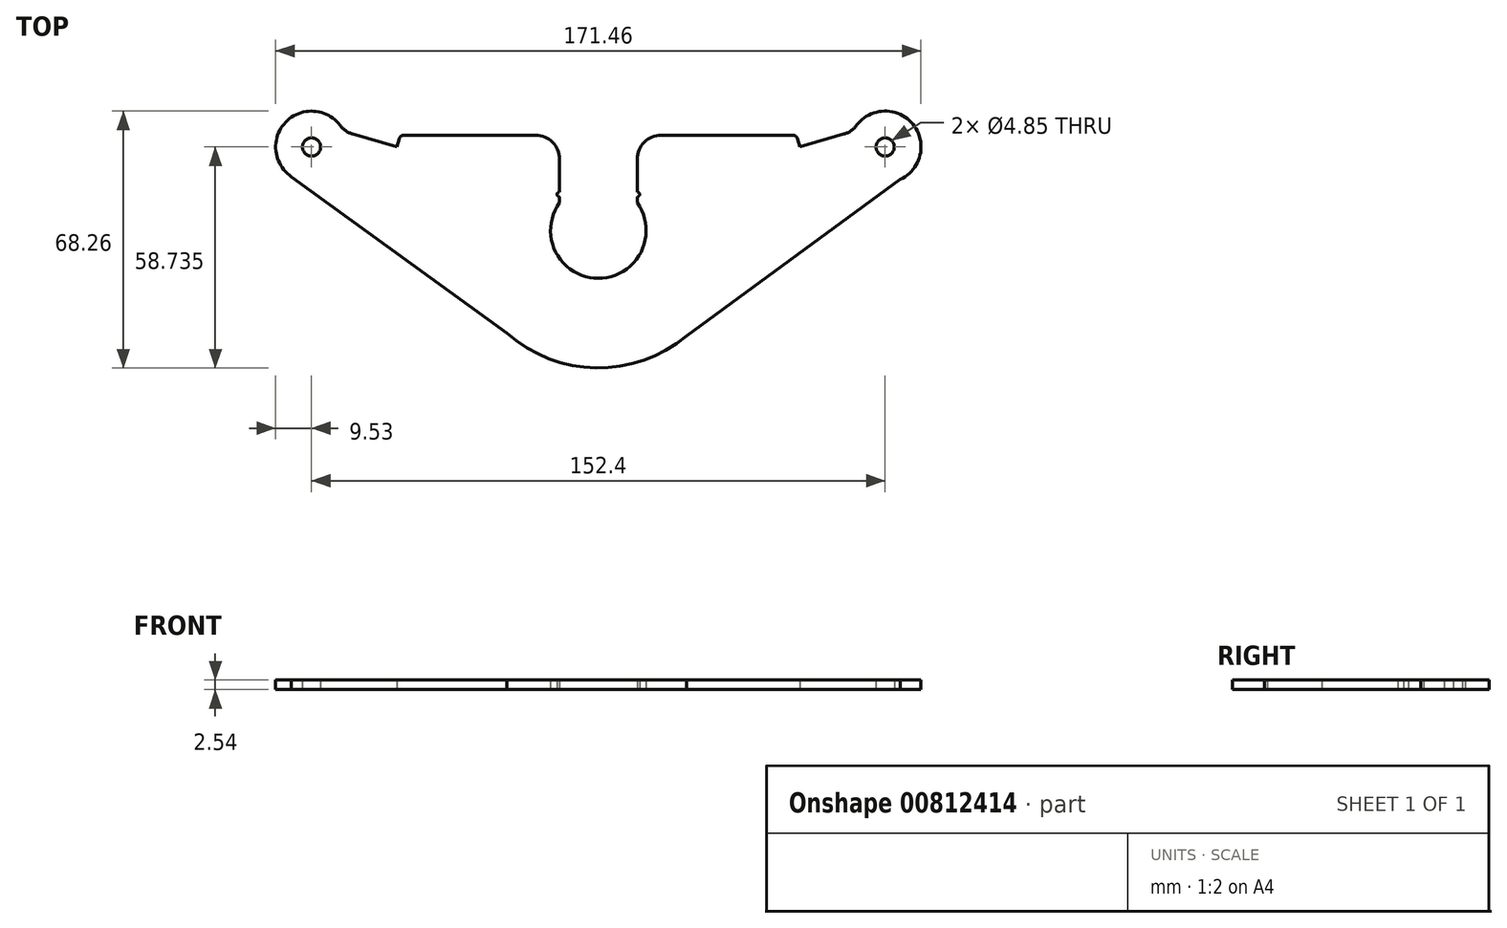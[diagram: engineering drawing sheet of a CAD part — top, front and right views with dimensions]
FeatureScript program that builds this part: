
annotation { "Feature Type Name" : "Feature", "Feature Type Description" : "" }
export const myFeature = defineFeature(function(context is Context, id is Id, definition is map)
    precondition{}
    {
        {
            var Q0;
            Q0=qCreatedBy(makeId("Top.planeOp"),FACE);
            var sketch = newSketch(context, id + "F0", { "sketchPlane" : qUnion([Q0])});
            skArc(sketch, "E0", {"start": v(-10.32, 7.4) * mm, "mid": v(0, -12.7) * mm, "end": v(10.32, 7.4) * mm});
            skCircle(sketch, "E1", {"center": v(-76.2, 22.23) * mm, "radius": 2.43 * mm});
            skCircle(sketch, "E2", {"center": v(76.2, 22.23) * mm, "radius": 2.43 * mm});
            skArc(sketch, "E3", {"start": v(-68.58, 27.94) * mm, "mid": v(-83.1, 28.8) * mm, "end": v(-81.53, 14.33) * mm});
            skArc(sketch, "E4", {"start": v(80.23, 13.6) * mm, "mid": v(83.6, 28.23) * mm, "end": v(68.58, 27.94) * mm});
            skArc(sketch, "E5", {"start": v(-24.33, -27.22) * mm, "mid": v(-0.62, -36.5) * mm, "end": v(23.39, -28.04) * mm});
            skLineSegment(sketch, "E6", {"start": v(-81.53, 14.33) * mm, "end": v(-24.33, -27.22) * mm});
            skLineSegment(sketch, "E7", {"start": v(23.39, -28.04) * mm, "end": v(83.2, 15.78) * mm});
            skLineSegment(sketch, "E8.0", {"start": v(-65.28, 25.65) * mm, "end": v(-53.54, 22.23) * mm});
            skLineSegment(sketch, "E9.0", {"start": v(53.54, 22.23) * mm, "end": v(65.28, 25.65) * mm});
            skLineSegment(sketch, "E10.left", {"start": v(10.32, 8.99) * mm, "end": v(10.32, 7.4) * mm});
            skLineSegment(sketch, "E10.right", {"start": v(-10.32, 9) * mm, "end": v(-10.32, 7.4) * mm});
            skPoint(sketch, "E10.top.end.orphan", {"position": v(-10.32, -39.66) * mm});
            skPoint(sketch, "E11.trimOffspring.end.orphan", {"position": v(10.32, -39.66) * mm});
            skPoint(sketch, "E10.bottom.end.orphan", {"position": v(-10.32, 39.66) * mm});
            skPoint(sketch, "E12.orphan", {"position": v(10.32, 39.66) * mm});
            skLineSegment(sketch, "E13", {"start": v(-10.32, 10.25) * mm, "end": v(-10.32, 18.98) * mm});
            skLineSegment(sketch, "E14", {"start": v(10.32, 10.26) * mm, "end": v(10.32, 18.98) * mm});
            skLineSegment(sketch, "E15", {"start": v(-52.9, 24.42) * mm, "end": v(-53.54, 22.23) * mm});
            skLineSegment(sketch, "E16", {"start": v(-16.67, 25.33) * mm, "end": v(-51.68, 25.33) * mm});
            skLineSegment(sketch, "E17", {"start": v(16.67, 25.33) * mm, "end": v(51.68, 25.33) * mm});
            skLineSegment(sketch, "E18", {"start": v(52.9, 24.42) * mm, "end": v(53.54, 22.23) * mm});
            skPoint(sketch, "E19.visualSharp", {"position": v(-67.6, 26.33) * mm});
            skArc(sketch, "E19.filletArc", {"start": v(-68.58, 27.94) * mm, "mid": v(-67.11, 26.53) * mm, "end": v(-65.28, 25.65) * mm});
            skPoint(sketch, "E20.visualSharp", {"position": v(67.6, 26.33) * mm});
            skArc(sketch, "E20.filletArc", {"start": v(65.28, 25.65) * mm, "mid": v(67.11, 26.53) * mm, "end": v(68.58, 27.94) * mm});
            skPoint(sketch, "E21.visualSharp", {"position": v(10.32, 25.33) * mm});
            skArc(sketch, "E21.filletArc", {"start": v(16.67, 25.33) * mm, "mid": v(12.18, 23.47) * mm, "end": v(10.32, 18.98) * mm});
            skPoint(sketch, "E22.visualSharp", {"position": v(-10.32, 25.33) * mm});
            skArc(sketch, "E22.filletArc", {"start": v(-10.32, 18.98) * mm, "mid": v(-12.18, 23.47) * mm, "end": v(-16.67, 25.33) * mm});
            skPoint(sketch, "E23.visualSharp", {"position": v(-52.63, 25.33) * mm});
            skArc(sketch, "E23.filletArc", {"start": v(-51.68, 25.33) * mm, "mid": v(-52.44, 25.08) * mm, "end": v(-52.9, 24.42) * mm});
            skPoint(sketch, "E24.visualSharp", {"position": v(52.64, 25.33) * mm});
            skArc(sketch, "E24.filletArc", {"start": v(52.9, 24.42) * mm, "mid": v(52.44, 25.08) * mm, "end": v(51.68, 25.33) * mm});
            skArc(sketch, "E25", {"start": v(-10.32, 10.25) * mm, "mid": v(-10.95, 9.62) * mm, "end": v(-10.32, 9) * mm});
            skArc(sketch, "E26", {"start": v(10.32, 8.99) * mm, "mid": v(10.95, 9.62) * mm, "end": v(10.32, 10.26) * mm});
            skSolve(sketch);
        }
        {
            var Q0;
            Q0 = qSketchRegion(id + "F0", true);
            extrude(context, id + "F1", {"entities" : qUnion([Q0]), "depth" : 2.54 * mm, "offsetDistance" : 25.4 * mm});
        }
    });
